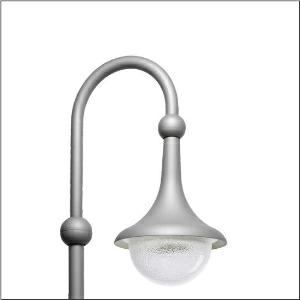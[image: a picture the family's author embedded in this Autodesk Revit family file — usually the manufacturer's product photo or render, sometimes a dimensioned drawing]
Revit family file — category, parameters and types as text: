
# Revit family: kleine_glocke___st1_2a_5xa1573k1b208_586f
name_source: partatom
category: Lighting Fixtures
units: mm (PartAtom-declared; Revit-internal decimal feet)

## family parameters
Cut with Voids When Loaded = No
Host = Face
Light Source = No
Part Type = Normal
Room Calculation Point = No
Round Connector Dimension = Use Diameter
Shared = No

## types (1)
- --- (1 x LED, 1750 lm, 13.2 W, 4000K)
    Apparent Load = 13 VA
    CIE Flux Codes = 28 64 93 98 100
    Color Rendering = 70
    Color Temperature = 4000K
    Default Elevation = 1800 mm
    Description = Small Bell, mast luminaire, primary light control with 3 zone facetted reflector, of plastic, aluminium vaporised, primary optical cover: enclosure, of PMMA, transparent structured, light distribution: ST1.2a, light emission: direct distribution, primary light characteristic: asymmetric, installation type: suspended mounting, LED, High Power LED, rated luminous flux: 1.750lm, luminous efficacy: 133lm/W, light colour: 740, colour temperature: 4000K, control gear: ECG Plus, control: flexible luminous flux parameterisation, time-dependent luminous flux control, constant luminous flux control, digital communication interface, power reduction, electronic power reduction, mains connection: 230..240V, AC, 50/60Hz, start of lifetime: 13W, end of service life: 14W, reduction: 7W, luminaire housing, bell-shaped, of glass-fibre reinforced polyester, coated, Siteco® metallic grey (DB 702S), please order curved mast extension separately, diameter: 430mm, height: 575mm, protection rating (complete): IP54, insulation class (complete): insulation class II (safety insulation), certification: CE, ENEC, VDE, impact resistance: IK07, standard-compliant lighting for roads and squares, packaging unit: 1 piece

Light Distribution: ST1.2a
    Height = 575 mm
    Lamp = 1 x LED
    Lamp Light Flux = 1750 lm
    Lamp Power = 13.2 W
    Lamp count = 1
    Length = 430 mm
    Luminous efficacy = 133 lm/W
    Manufacturer = Siteco
    ModVariant = No
    Model = 5XA1573K1B208
    Number of Poles = 1
    OnlyDefault = Yes
    Power Factor = 1
    Product Name = Kleine Glocke | ST1.2a
    Product group = mast luminaire | pylon annexe
    ProductGroupID = 6201
    Protection Class = Protection class II
    Protection Degree = IP 54
    RLX_Detail_Level = 1
    RLX_Emergency_Light_Flux = 0 lm
    RLX_Emergency_Type = 0
    RLX_Emergency_Type_DB = No
    RlxData = <blob elided: 52061 chars, md5=87f34b79>
    Socket = socket
    Standby Power = 0 W
    System Light Flux = 1750 lm
    System Power = 13 W
    Type Comments = factory setting: luminous flux: 100 % | dim-lin: 254 | 249 mA
    Type Image = l_1284392.jpg
    URL = http://relux.com
    VarID = @adj_137475
    Voltage = 0 V
    Weight = 0.00 kg
    Width = 0 mm  [stored 0 ft]

note: [stored X ft] marks values corroborated as IEEE doubles in the binary element streams (Revit-internal decimal feet)

## geometry (parser evidence)
native form markers: Blend x4, Sweep x12
no freeform markers — native parametric forms only
